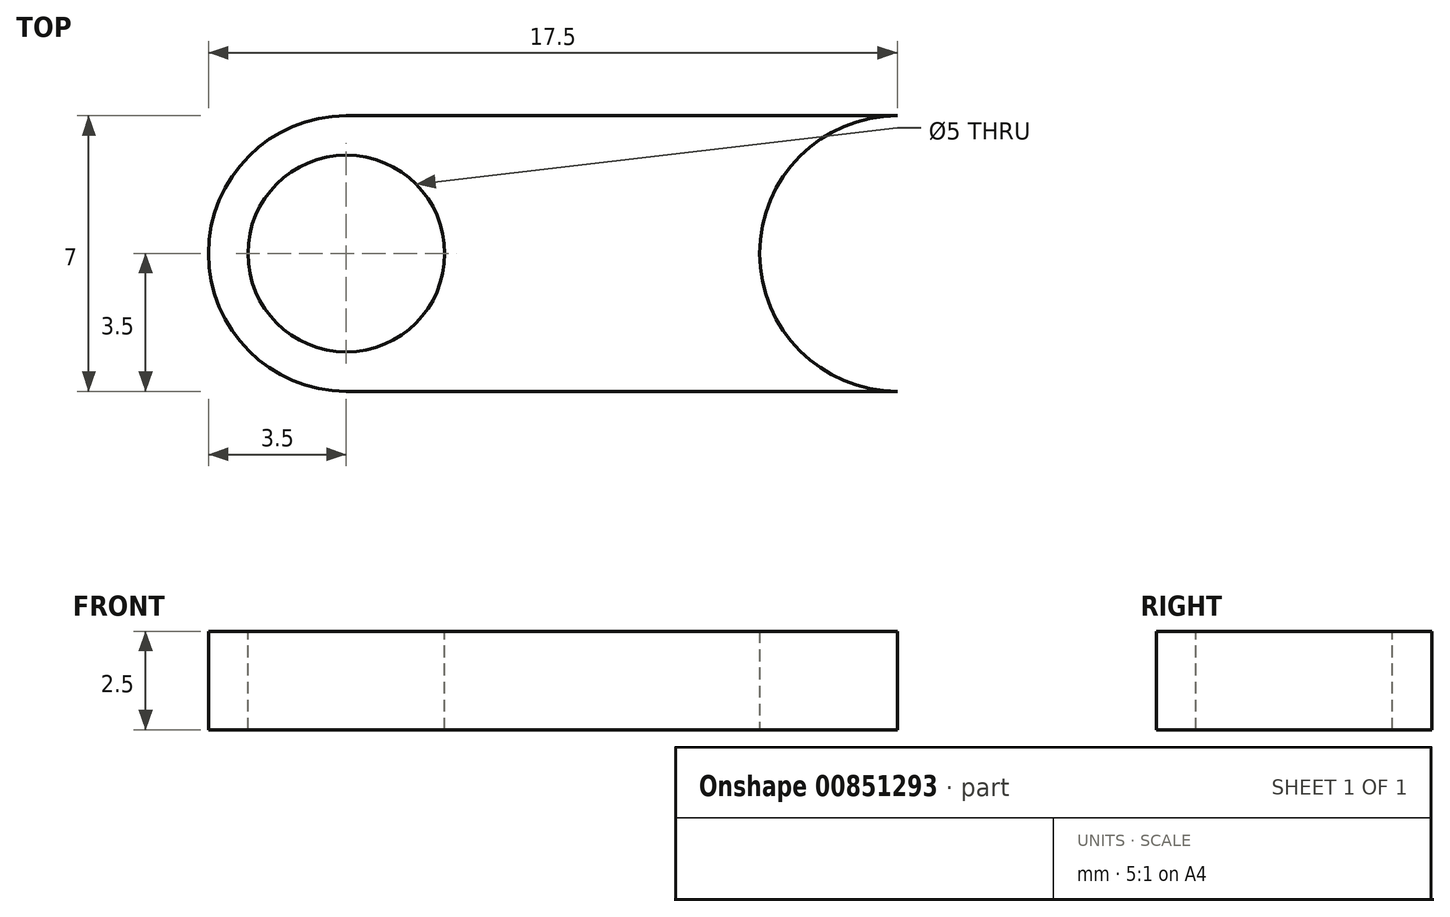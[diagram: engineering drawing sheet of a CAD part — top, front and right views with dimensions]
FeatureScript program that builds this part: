
annotation { "Feature Type Name" : "Feature", "Feature Type Description" : "" }
export const myFeature = defineFeature(function(context is Context, id is Id, definition is map)
    precondition{}
    {
        {
            var Q0;
            Q0=qCreatedBy(makeId("Top.planeOp"),FACE);
            var sketch = newSketch(context, id + "F0", { "sketchPlane" : qUnion([Q0])});
            skCircle(sketch, "E0", {"center": v(-7, 0) * mm, "radius": 3.5 * mm});
            skLineSegment(sketch, "E1.bottom", {"start": v(-7, 3.5) * mm, "end": v(0, 3.5) * mm});
            skLineSegment(sketch, "E1.top", {"start": v(-7, -3.5) * mm, "end": v(0, -3.5) * mm});
            skLineSegment(sketch, "E1.left", {"start": v(-7, 3.5) * mm, "end": v(-7, -3.5) * mm});
            skLineSegment(sketch, "E1.right", {"start": v(0, 3.5) * mm, "end": v(0, -3.5) * mm});
            skLineSegment(sketch, "E2.MirrorCS", {"start": v(7, 3.5) * mm, "end": v(0, 3.5) * mm});
            skLineSegment(sketch, "E3.MirrorCS", {"start": v(7, -3.5) * mm, "end": v(0, -3.5) * mm});
            skCircle(sketch, "E4.MirrorC", {"center": v(7, 0) * mm, "radius": 3.5 * mm});
            skSolve(sketch);
        }
        {
            var Q0;
            {var subQ0=sQuery(id+"F0.wireOp",EDGE,"E1.left");Q0=makeQuery(id+"F0.imprint","IMPRINT",FACE,{"disambiguationData":[TD([[makeQuery(id+"F0.imprint","IMPRINT",EDGE,{"derivedFrom":subQ0}),-1.0]])]});}
            var Q1;
            {var subQ0=sQuery(id+"F0.wireOp",EDGE,"E1.left");Q1=makeQuery(id+"F0.imprint","IMPRINT",FACE,{"disambiguationData":[TD([[makeQuery(id+"F0.imprint","IMPRINT",EDGE,{"derivedFrom":subQ0}),1.0]])]});}
            var Q2;
            {var subQ1=sQuery(id+"F0.wireOp",EDGE,"E1.bottom");Q2=makeQuery(id+"F0.imprint","IMPRINT",FACE,{"disambiguationData":[TD([[makeQuery(id+"F0.imprint","IMPRINT",EDGE,{"derivedFrom":subQ1}),-1.0]])]});}
            var Q3;
            Q3=makeQuery(id+"F0.imprint","IMPRINT",FACE,{"disambiguationData":[TD([[makeQuery(id+"F0.imprint","IMPRINT",EDGE,{"derivedFrom":sQuery(id+"F0.wireOp",EDGE,"E1.right")}),1.0]])]});
            var Q4;
            {var subQ0=sQuery(id+"F0.wireOp",EDGE,"E4.MirrorC");var subQ1=makeQuery(id+"F0.imprint","INTERSECT",VERTEX,{"derivedFrom":[sQuery(id+"F0.wireOp",EDGE,"E2.MirrorCS"),subQ0]});Q4=makeQuery(id+"F0.imprint","IMPRINT",FACE,{"disambiguationData":[TD([[makeQuery(id+"F0.imprint","IMPRINT",EDGE,{"disambiguationData":[TD([[subQ1,-1.0]])],"derivedFrom":subQ0}),-1.0]])]});}
            extrude(context, id + "F1", {"entities" : qUnion([Q0, Q1, Q2, Q3, Q4]), "depth" : 2.5 * mm, "offsetDistance" : 25 * mm});
        }
        {
            var Q0;
            Q0=makeQuery(id+"F1.opExtrude","CAP_FACE",FACE,{"disambiguationData":[OSD([sQuery(id+"F0.wireOp",EDGE,"E0"),sQuery(id+"F0.wireOp",EDGE,"E1.bottom"),sQuery(id+"F0.wireOp",EDGE,"E1.top"),sQuery(id+"F0.wireOp",EDGE,"E2.MirrorCS"),sQuery(id+"F0.wireOp",EDGE,"E3.MirrorCS"),sQuery(id+"F0.wireOp",EDGE,"E4.MirrorC")])],"isStart":false});
            var sketch = newSketch(context, id + "F2", { "sketchPlane" : qUnion([Q0])});
            skCircle(sketch, "E5", {"center": v(-7, 0) * mm, "radius": 2.5 * mm});
            skCircle(sketch, "E6", {"center": v(7, 0) * mm, "radius": 2.5 * mm});
            skSolve(sketch);
        }
        {
            var Q0;
            Q0=makeQuery(id+"F2.imprint","IMPRINT",FACE,{"disambiguationData":[TD([[makeQuery(id+"F2.imprint","IMPRINT",EDGE,{"derivedFrom":sQuery(id+"F2.wireOp",EDGE,"E5")}),1.0]])]});
            var Q1;
            Q1=makeQuery(id+"F2.imprint","IMPRINT",FACE,{"disambiguationData":[TD([[makeQuery(id+"F2.imprint","IMPRINT",EDGE,{"derivedFrom":sQuery(id+"F2.wireOp",EDGE,"E6")}),1.0]])]});
            extrude(context, id + "F3", {"entities" : qUnion([Q0, Q1]), "operationType" : NewBodyOperationType.REMOVE, "oppositeDirection" : true, "depth" : 25 * mm, "offsetDistance" : 25 * mm});
        }
    });
